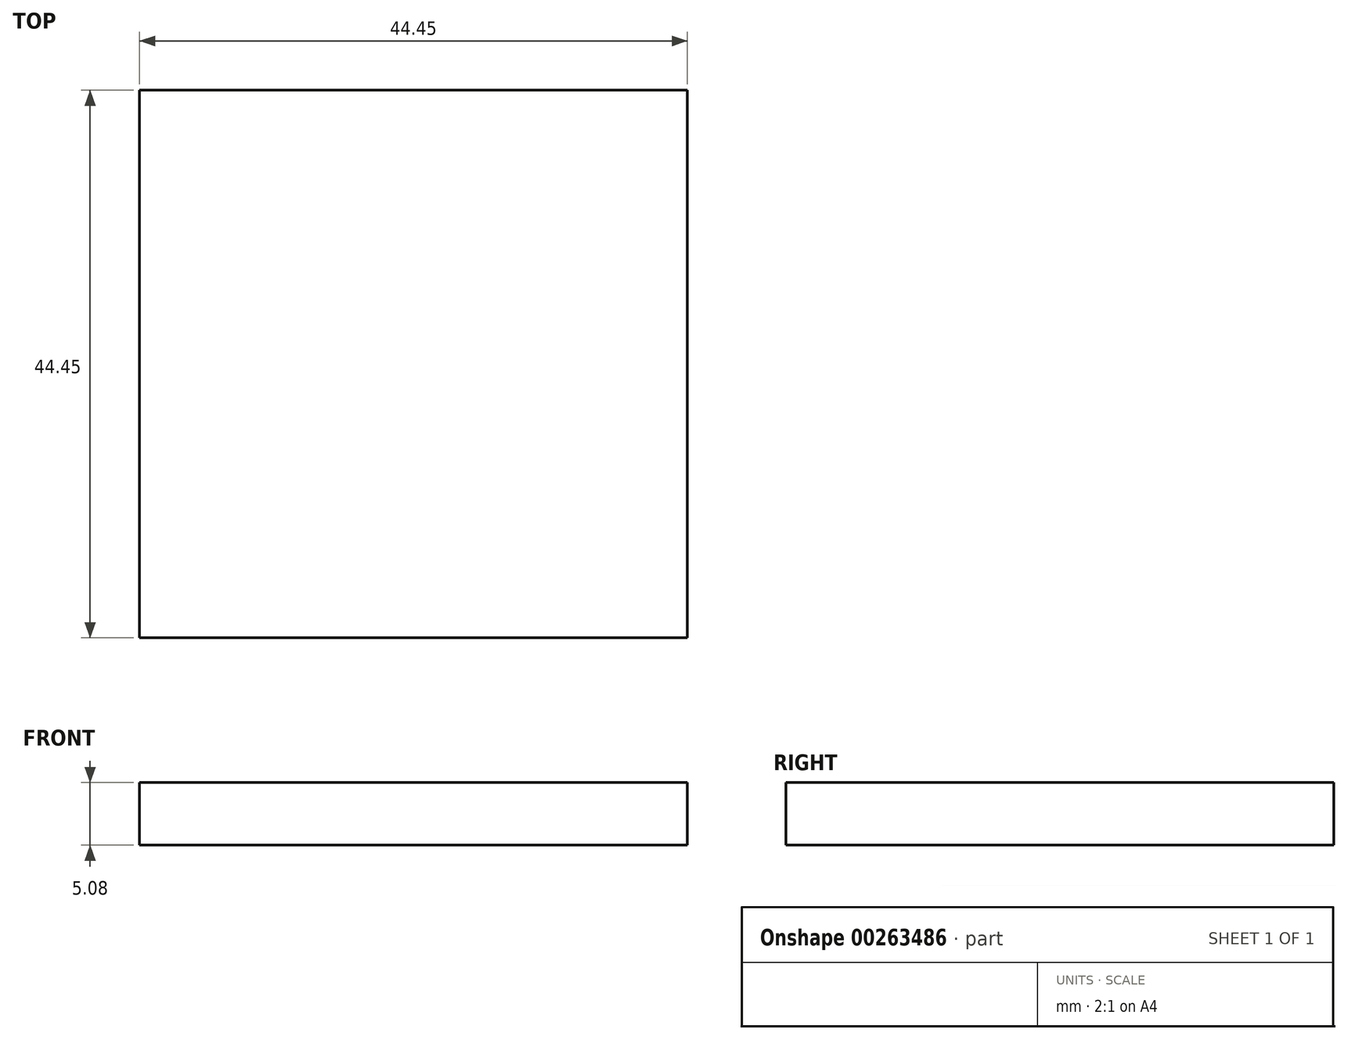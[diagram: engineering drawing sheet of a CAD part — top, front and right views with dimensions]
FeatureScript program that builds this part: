
annotation { "Feature Type Name" : "Feature", "Feature Type Description" : "" }
export const myFeature = defineFeature(function(context is Context, id is Id, definition is map)
    precondition{}
    {
        {
            var Q0;
            Q0=qCreatedBy(makeId("Top.planeOp"),FACE);
            var sketch = newSketch(context, id + "F0", { "sketchPlane" : qUnion([Q0])});
            skLineSegment(sketch, "E0.bottom", {"start": v(-50.26, -4.43) * mm, "end": v(-5.8, -4.43) * mm});
            skLineSegment(sketch, "E0.top", {"start": v(-50.26, -48.88) * mm, "end": v(-5.8, -48.88) * mm});
            skLineSegment(sketch, "E0.left", {"start": v(-50.26, -4.43) * mm, "end": v(-50.26, -48.88) * mm});
            skLineSegment(sketch, "E0.right", {"start": v(-5.8, -4.43) * mm, "end": v(-5.8, -48.88) * mm});
            skSolve(sketch);
        }
        {
            var Q0;
            Q0 = qSketchRegion(id + "F0", true);
            extrude(context, id + "F1", {"entities" : qUnion([Q0]), "depth" : 5.08 * mm});
        }
    });
